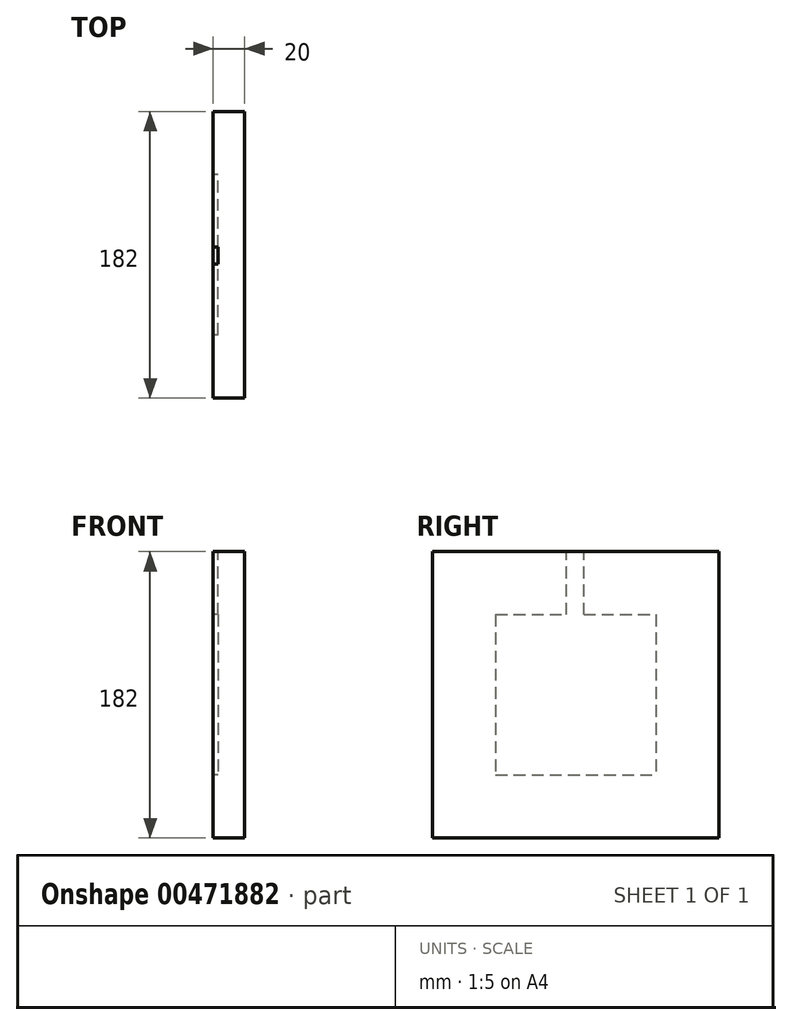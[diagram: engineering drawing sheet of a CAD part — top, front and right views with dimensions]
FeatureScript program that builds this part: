
annotation { "Feature Type Name" : "Feature", "Feature Type Description" : "" }
export const myFeature = defineFeature(function(context is Context, id is Id, definition is map)
    precondition{}
    {
        {
            var Q0;
            Q0=qCreatedBy(makeId("Right.planeOp"),FACE);
            var sketch = newSketch(context, id + "F0", { "sketchPlane" : qUnion([Q0])});
            skLineSegment(sketch, "E0.bottom", {"start": v(0, 0) * mm, "end": v(102, 0) * mm});
            skLineSegment(sketch, "E0.top", {"start": v(0, -102) * mm, "end": v(102, -102) * mm});
            skLineSegment(sketch, "E0.left", {"start": v(0, 0) * mm, "end": v(0, -102) * mm});
            skLineSegment(sketch, "E0.right", {"start": v(102, 0) * mm, "end": v(102, -102) * mm});
            skLineSegment(sketch, "E1.0", {"start": v(-40, 40) * mm, "end": v(142, 40) * mm});
            skLineSegment(sketch, "E1.1", {"start": v(-40, 40) * mm, "end": v(-40, -142) * mm});
            skLineSegment(sketch, "E1.2", {"start": v(-40, -142) * mm, "end": v(142, -142) * mm});
            skLineSegment(sketch, "E1.3", {"start": v(142, 40) * mm, "end": v(142, -142) * mm});
            skSolve(sketch);
        }
        {
            var Q0;
            Q0=makeQuery(id+"F0.imprint","IMPRINT",FACE,{"disambiguationData":[TD([[makeQuery(id+"F0.imprint","IMPRINT",EDGE,{"derivedFrom":sQuery(id+"F0.wireOp",EDGE,"E0.bottom")}),1.0]])]});
            var Q1;
            Q1=makeQuery(id+"F0.imprint","IMPRINT",FACE,{"disambiguationData":[TD([[makeQuery(id+"F0.imprint","IMPRINT",EDGE,{"derivedFrom":sQuery(id+"F0.wireOp",EDGE,"E0.bottom")}),-1.0]])]});
            extrude(context, id + "F1", {"entities" : qUnion([Q0, Q1]), "depth" : 20 * mm});
        }
        {
            var Q0;
            Q0=makeQuery(id+"F0.imprint","IMPRINT",FACE,{"disambiguationData":[TD([[makeQuery(id+"F0.imprint","IMPRINT",EDGE,{"derivedFrom":sQuery(id+"F0.wireOp",EDGE,"E0.bottom")}),-1.0]])]});
            extrude(context, id + "F2", {"entities" : qUnion([Q0]), "operationType" : NewBodyOperationType.REMOVE, "depth" : 3 * mm});
        }
        {
            var Q0;
            Q0=makeQuery(id+"F0.imprint","IMPRINT",FACE,{"disambiguationData":[TD([[makeQuery(id+"F0.imprint","IMPRINT",EDGE,{"derivedFrom":sQuery(id+"F0.wireOp",EDGE,"E0.bottom")}),1.0]])]});
            var sketch = newSketch(context, id + "F3", { "sketchPlane" : qUnion([Q0])});
            skLineSegment(sketch, "E2.bottom", {"start": v(45, 0) * mm, "end": v(56, 0) * mm});
            skLineSegment(sketch, "E2.top", {"start": v(45, 40) * mm, "end": v(56, 40) * mm});
            skLineSegment(sketch, "E2.left", {"start": v(45, 0) * mm, "end": v(45, 40) * mm});
            skLineSegment(sketch, "E2.right", {"start": v(56, 0) * mm, "end": v(56, 40) * mm});
            skSolve(sketch);
        }
        {
            var Q0;
            Q0=makeQuery(id+"F3.imprint","IMPRINT",FACE,{"disambiguationData":[TD([[makeQuery(id+"F3.imprint","IMPRINT",EDGE,{"derivedFrom":sQuery(id+"F3.wireOp",EDGE,"E2.bottom")}),1.0]])]});
            extrude(context, id + "F4", {"entities" : qUnion([Q0]), "operationType" : NewBodyOperationType.REMOVE, "depth" : 3 * mm});
        }
    });
